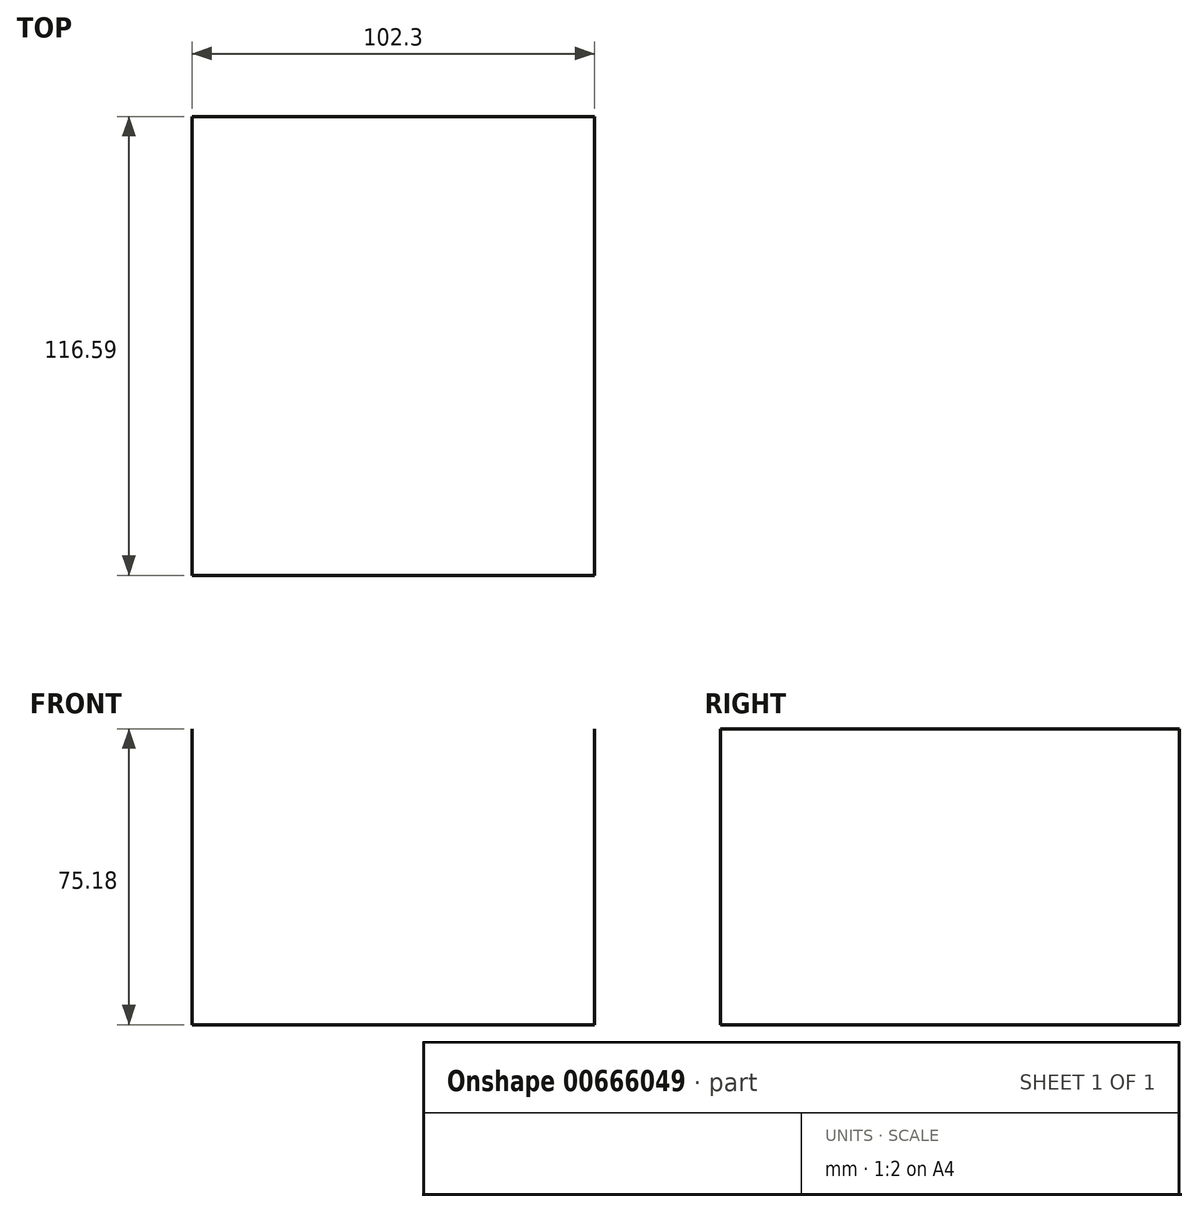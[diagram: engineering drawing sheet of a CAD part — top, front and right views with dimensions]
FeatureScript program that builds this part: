
annotation { "Feature Type Name" : "Feature", "Feature Type Description" : "" }
export const myFeature = defineFeature(function(context is Context, id is Id, definition is map)
    precondition{}
    {
        {
            var Q0;
            Q0=qCreatedBy(makeId("Front.planeOp"),FACE);
            var sketch = newSketch(context, id + "F0", { "sketchPlane" : qUnion([Q0])});
            skLineSegment(sketch, "E0.bottom", {"start": v(-51.15, -37.59) * mm, "end": v(51.15, -37.59) * mm});
            skLineSegment(sketch, "E0.top", {"start": v(-51.15, 37.59) * mm, "end": v(51.15, 37.59) * mm});
            skLineSegment(sketch, "E0.left", {"start": v(-51.15, -37.59) * mm, "end": v(-51.15, 37.59) * mm});
            skLineSegment(sketch, "E0.right", {"start": v(51.15, -37.59) * mm, "end": v(51.15, 37.59) * mm});
            skPoint(sketch, "E0.middle", {"position": v(0, 0) * mm});
            skSolve(sketch);
        }
        {
            var Q0;
            Q0=sQuery(id+"F0.wireOp",EDGE,"E0.bottom");
            var Q1;
            Q1=sQuery(id+"F0.wireOp",EDGE,"E0.left");
            var Q2;
            Q2=sQuery(id+"F0.wireOp",EDGE,"E0.right");
            extrude(context, id + "F1", {"bodyType" : ToolBodyType.SURFACE, "surfaceEntities" : qUnion([Q0, Q1, Q2]), "depth" : 116.6 * mm, "offsetDistance" : 25.4 * mm});
        }
    });
